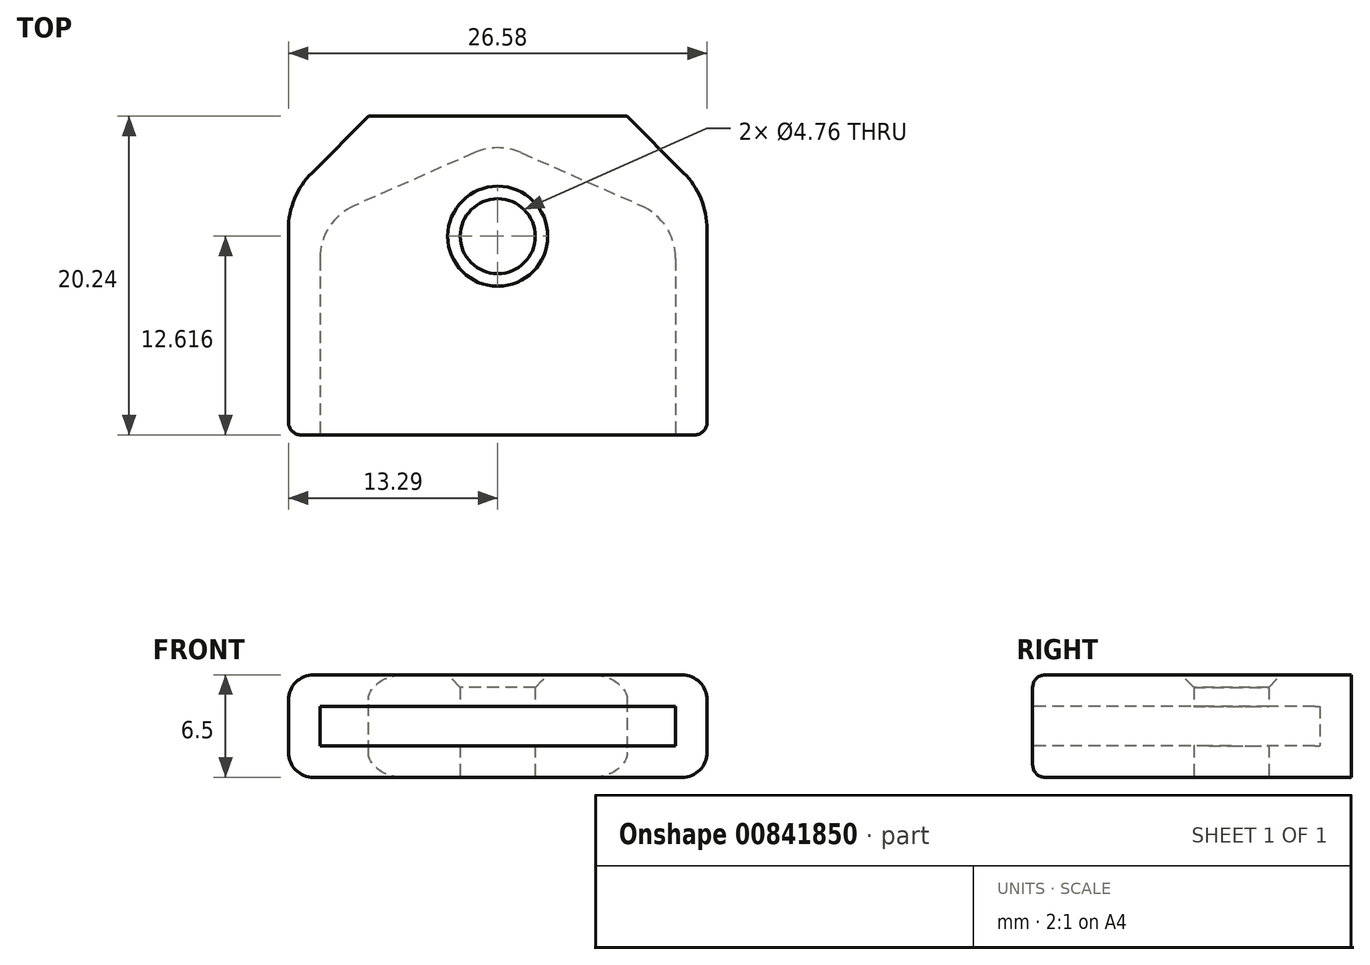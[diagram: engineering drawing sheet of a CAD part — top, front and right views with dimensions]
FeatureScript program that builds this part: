
annotation { "Feature Type Name" : "Feature", "Feature Type Description" : "" }
export const myFeature = defineFeature(function(context is Context, id is Id, definition is map)
    precondition{}
    {
        {
            var Q0;
            Q0=qCreatedBy(makeId("Top.planeOp"),FACE);
            var sketch = newSketch(context, id + "F0", { "sketchPlane" : qUnion([Q0])});
            skLineSegment(sketch, "E0", {"start": v(-1.28, 11.87) * mm, "end": v(-8.9, 8.5) * mm});
            skLineSegment(sketch, "E1", {"start": v(1.28, 11.87) * mm, "end": v(8.9, 8.5) * mm});
            skLineSegment(sketch, "E2", {"start": v(0, 12.43) * mm, "end": v(0, -39.93) * mm, "construction": true});
            skLineSegment(sketch, "E3", {"start": v(-10.8, 5.6) * mm, "end": v(-10.8, -5.6) * mm});
            skLineSegment(sketch, "E4", {"start": v(-8.9, -8.5) * mm, "end": v(-7.33, -9.2) * mm, "construction": true});
            skLineSegment(sketch, "E5", {"start": v(-6.39, -10.65) * mm, "end": v(-6.39, -12) * mm, "construction": true});
            skLineSegment(sketch, "E6", {"start": v(-6.39, -12) * mm, "end": v(-4.27, -12) * mm, "construction": true});
            skLineSegment(sketch, "E7", {"start": v(-4.27, -12) * mm, "end": v(-4.27, -39.93) * mm, "construction": true});
            skLineSegment(sketch, "E8", {"start": v(10.8, 5.6) * mm, "end": v(10.8, -5.6) * mm});
            skLineSegment(sketch, "E9", {"start": v(-10.8, 0) * mm, "end": v(0, 0) * mm, "construction": true});
            skLineSegment(sketch, "E10", {"start": v(0, 0) * mm, "end": v(10.8, 0) * mm, "construction": true});
            skLineSegment(sketch, "E11", {"start": v(8.9, -8.5) * mm, "end": v(7.33, -9.2) * mm, "construction": true});
            skLineSegment(sketch, "E12", {"start": v(6.39, -10.65) * mm, "end": v(6.39, -12) * mm, "construction": true});
            skLineSegment(sketch, "E13", {"start": v(6.39, -12) * mm, "end": v(4.27, -12) * mm, "construction": true});
            skLineSegment(sketch, "E14", {"start": v(4.27, -12) * mm, "end": v(4.27, -39.93) * mm, "construction": true});
            skLineSegment(sketch, "E15", {"start": v(-4.27, -39.93) * mm, "end": v(4.27, -39.93) * mm, "construction": true});
            skPoint(sketch, "E16.visualSharp", {"position": v(0, 12.43) * mm});
            skArc(sketch, "E16.filletArc", {"start": v(1.28, 11.87) * mm, "mid": v(0, 12.14) * mm, "end": v(-1.28, 11.87) * mm});
            skPoint(sketch, "E17.visualSharp", {"position": v(-10.8, 7.67) * mm});
            skArc(sketch, "E17.filletArc", {"start": v(-8.9, 8.5) * mm, "mid": v(-10.28, 7.33) * mm, "end": v(-10.8, 5.6) * mm});
            skPoint(sketch, "E18.visualSharp", {"position": v(10.8, 7.67) * mm});
            skArc(sketch, "E18.filletArc", {"start": v(10.8, 5.6) * mm, "mid": v(10.28, 7.33) * mm, "end": v(8.9, 8.5) * mm});
            skPoint(sketch, "E19", {"position": v(0, 12.14) * mm});
            skPoint(sketch, "E20.visualSharp", {"position": v(10.8, -7.67) * mm});
            skArc(sketch, "E20.filletArc", {"start": v(8.9, -8.5) * mm, "mid": v(10.28, -7.33) * mm, "end": v(10.8, -5.6) * mm, "construction": true});
            skPoint(sketch, "E21.visualSharp", {"position": v(-10.8, -7.67) * mm});
            skArc(sketch, "E21.filletArc", {"start": v(-10.8, -5.6) * mm, "mid": v(-10.28, -7.33) * mm, "end": v(-8.9, -8.5) * mm, "construction": true});
            skPoint(sketch, "E22.visualSharp", {"position": v(-6.39, -9.61) * mm});
            skArc(sketch, "E22.filletArc", {"start": v(-6.39, -10.65) * mm, "mid": v(-6.65, -9.78) * mm, "end": v(-7.33, -9.2) * mm, "construction": true});
            skPoint(sketch, "E23.visualSharp", {"position": v(6.39, -9.61) * mm});
            skArc(sketch, "E23.filletArc", {"start": v(7.33, -9.2) * mm, "mid": v(6.65, -9.78) * mm, "end": v(6.39, -10.65) * mm, "construction": true});
            skLineSegment(sketch, "E24", {"start": v(-10.8, -5.6) * mm, "end": v(10.8, -5.6) * mm});
            skLineSegment(sketch, "E25.0", {"start": v(-11.3, 5.6) * mm, "end": v(-11.3, -5.6) * mm});
            skArc(sketch, "E25.1", {"start": v(-9.1, 8.96) * mm, "mid": v(-10.7, 7.6) * mm, "end": v(-11.3, 5.6) * mm});
            skLineSegment(sketch, "E25.2", {"start": v(-1.48, 12.32) * mm, "end": v(-9.1, 8.96) * mm});
            skLineSegment(sketch, "E25.3", {"start": v(11.3, 5.6) * mm, "end": v(11.3, -5.6) * mm});
            skArc(sketch, "E25.4", {"start": v(11.3, 5.6) * mm, "mid": v(10.7, 7.6) * mm, "end": v(9.1, 8.96) * mm});
            skLineSegment(sketch, "E25.5", {"start": v(1.48, 12.32) * mm, "end": v(9.1, 8.96) * mm});
            skArc(sketch, "E25.6", {"start": v(1.48, 12.32) * mm, "mid": v(0, 12.64) * mm, "end": v(-1.48, 12.32) * mm});
            skLineSegment(sketch, "E26", {"start": v(-11.3, -5.6) * mm, "end": v(11.3, -5.6) * mm});
            skSolve(sketch);
        }
        {
            var Q0;
            Q0=makeQuery(id+"F0.imprint","IMPRINT",FACE,{"disambiguationData":[TD([[makeQuery(id+"F0.imprint","IMPRINT",EDGE,{"derivedFrom":sQuery(id+"F0.wireOp",EDGE,"E0")}),1.0]])]});
            var Q1;
            Q1=makeQuery(id+"F0.imprint","IMPRINT",FACE,{"disambiguationData":[TD([[makeQuery(id+"F0.imprint","IMPRINT",EDGE,{"derivedFrom":sQuery(id+"F0.wireOp",EDGE,"E0")}),-1.0]])]});
            extrude(context, id + "F1", {"entities" : qUnion([Q0, Q1]), "depth" : 2.5 * mm, "offsetDistance" : 25.4 * mm, "symmetric" : true});
        }
        {
            var Q0;
            Q0=makeQuery(id+"F1.opExtrude","SWEPT_FACE",FACE,{"disambiguationData":[OSD([sQuery(id+"F0.wireOp",EDGE,"E26")])]});
            shell(context, id + "F2", {"entities" : qUnion([Q0]), "thickness" : 2 * mm, "oppositeDirection" : true});
        }
        {
            var Q0;
            Q0=makeQuery(id+"F1.opExtrude","CAP_FACE",FACE,{"disambiguationData":[OSD([sQuery(id+"F0.wireOp",EDGE,"E25.0"),sQuery(id+"F0.wireOp",EDGE,"E25.1"),sQuery(id+"F0.wireOp",EDGE,"E25.2"),sQuery(id+"F0.wireOp",EDGE,"E25.3"),sQuery(id+"F0.wireOp",EDGE,"E25.4"),sQuery(id+"F0.wireOp",EDGE,"E25.5"),sQuery(id+"F0.wireOp",EDGE,"E25.6"),sQuery(id+"F0.wireOp",EDGE,"E26")])],"isStart":true});
            var sketch = newSketch(context, id + "F3", { "sketchPlane" : qUnion([Q0])});
            skCircle(sketch, "E27", {"center": v(0, -7.02) * mm, "radius": 2.38 * mm});
            skSolve(sketch);
        }
        {
            var Q0;
            Q0=makeQuery(id+"F3.imprint","IMPRINT",FACE,{"disambiguationData":[TD([[makeQuery(id+"F3.imprint","IMPRINT",EDGE,{"derivedFrom":sQuery(id+"F3.wireOp",EDGE,"E27")}),1.0]])]});
            extrude(context, id + "F4", {"entities" : qUnion([Q0]), "operationType" : NewBodyOperationType.REMOVE, "endBound" : BoundingType.THROUGH_ALL, "oppositeDirection" : true, "depth" : 25.4 * mm, "offsetDistance" : 25.4 * mm});
        }
        {
            var Q0;
            Q0=qCreatedBy(makeId("Top.planeOp"),FACE);
            var sketch = newSketch(context, id + "F5", { "sketchPlane" : qUnion([Q0])});
            skLineSegment(sketch, "E28.0", {"start": v(-2.3, 14.15) * mm, "end": v(-9.91, 10.8) * mm});
            skArc(sketch, "E29.0", {"start": v(-9.91, 10.8) * mm, "mid": v(-12.37, 8.7) * mm, "end": v(-13.3, 5.6) * mm});
            skArc(sketch, "E30.0", {"start": v(2.3, 14.15) * mm, "mid": v(0, 14.64) * mm, "end": v(-2.3, 14.15) * mm});
            skLineSegment(sketch, "E31.0", {"start": v(2.3, 14.15) * mm, "end": v(9.91, 10.8) * mm});
            skArc(sketch, "E32.0", {"start": v(13.3, 5.6) * mm, "mid": v(12.37, 8.7) * mm, "end": v(9.91, 10.8) * mm});
            skLineSegment(sketch, "E33", {"start": v(-13.3, 5.6) * mm, "end": v(-13.3, 14.64) * mm});
            skLineSegment(sketch, "E34", {"start": v(-13.3, 14.64) * mm, "end": v(0, 14.64) * mm});
            skPoint(sketch, "E34.endSnap0", {"position": v(0, 14.64) * mm});
            skLineSegment(sketch, "E35", {"start": v(0, 14.64) * mm, "end": v(13.3, 14.64) * mm});
            skLineSegment(sketch, "E36", {"start": v(13.3, 14.64) * mm, "end": v(13.3, 5.6) * mm});
            skSolve(sketch);
        }
        {
            var Q0;
            {var subQ1=sQuery(id+"F5.wireOp",EDGE,"E28.0");Q0=makeQuery(id+"F5.imprint","IMPRINT",FACE,{"disambiguationData":[TD([[makeQuery(id+"F5.imprint","IMPRINT",EDGE,{"derivedFrom":subQ1}),-1.0]])]});}
            var Q1;
            {var subQ1=sQuery(id+"F5.wireOp",EDGE,"E31.0");Q1=makeQuery(id+"F5.imprint","IMPRINT",FACE,{"disambiguationData":[TD([[makeQuery(id+"F5.imprint","IMPRINT",EDGE,{"derivedFrom":subQ1}),1.0]])]});}
            extrude(context, id + "F6", {"entities" : qUnion([Q0, Q1]), "operationType" : NewBodyOperationType.ADD, "depth" : 6.5 * mm, "offsetDistance" : 25.4 * mm, "symmetric" : true});
        }
        {
            var Q0;
            Q0=makeQuery(id+"F6.opExtrude","SWEPT_EDGE",EDGE,{"disambiguationData":[OSD([sQuery(id+"F5.wireOp",EDGE,"E33"),sQuery(id+"F5.wireOp",EDGE,"E34")])]});
            var Q1;
            Q1=makeQuery(id+"F6.opExtrude","SWEPT_EDGE",EDGE,{"disambiguationData":[OSD([sQuery(id+"F5.wireOp",EDGE,"E35"),sQuery(id+"F5.wireOp",EDGE,"E36")])]});
            chamfer(context, id + "F7", {"entities" : qUnion([Q0, Q1]), "width" : 5.08 * mm, "tangentPropagation" : true});
        }
        {
            var Q0;
            {var subQ0=sQuery(id+"F5.wireOp",EDGE,"E33");Q0=makeQuery(id+"F7.opChamfer","BLEND_EDGE",EDGE,{"blendedFrom":[makeQuery(id+"F6.opExtrude","SWEPT_EDGE",EDGE,{"disambiguationData":[OSD([subQ0,sQuery(id+"F5.wireOp",EDGE,"E34")])]}),makeQuery(id+"F6.boolean.opBoolean","MERGE",FACE,{"derivedFrom":[makeQuery(id+"F1.opExtrude","SWEPT_FACE",FACE,{"disambiguationData":[OSD([sQuery(id+"F0.wireOp",EDGE,"E25.0")])]}),makeQuery(id+"F6.opExtrude","SWEPT_FACE",FACE,{"disambiguationData":[OSD([subQ0])]})]})],"blendedInto":[makeQuery(id+"F6.boolean.opBoolean","MERGE",FACE,{"derivedFrom":[makeQuery(id+"F1.opExtrude","SWEPT_FACE",FACE,{"disambiguationData":[OSD([sQuery(id+"F0.wireOp",EDGE,"E25.0")])]}),makeQuery(id+"F6.opExtrude","SWEPT_FACE",FACE,{"disambiguationData":[OSD([subQ0])]})]})]});}
            var Q1;
            {var subQ0=sQuery(id+"F5.wireOp",EDGE,"E36");Q1=makeQuery(id+"F7.opChamfer","BLEND_EDGE",EDGE,{"blendedFrom":[makeQuery(id+"F6.opExtrude","SWEPT_EDGE",EDGE,{"disambiguationData":[OSD([sQuery(id+"F5.wireOp",EDGE,"E35"),subQ0])]}),makeQuery(id+"F6.boolean.opBoolean","MERGE",FACE,{"derivedFrom":[makeQuery(id+"F1.opExtrude","SWEPT_FACE",FACE,{"disambiguationData":[OSD([sQuery(id+"F0.wireOp",EDGE,"E25.3")])]}),makeQuery(id+"F6.opExtrude","SWEPT_FACE",FACE,{"disambiguationData":[OSD([subQ0])]})]})],"blendedInto":[makeQuery(id+"F6.boolean.opBoolean","MERGE",FACE,{"derivedFrom":[makeQuery(id+"F1.opExtrude","SWEPT_FACE",FACE,{"disambiguationData":[OSD([sQuery(id+"F0.wireOp",EDGE,"E25.3")])]}),makeQuery(id+"F6.opExtrude","SWEPT_FACE",FACE,{"disambiguationData":[OSD([subQ0])]})]})]});}
            fillet(context, id + "F8", {"entities" : qUnion([Q0, Q1]), "radius" : 5.08 * mm, "tangentPropagation" : true, "allowEdgeOverflow" : false});
        }
        {
            var Q0;
            Q0=makeQuery(id+"F6.boolean.opBoolean","MERGE",EDGE,{"derivedFrom":[makeQuery(id+"F1.opExtrude","CAP_EDGE",EDGE,{"disambiguationData":[OSD([sQuery(id+"F0.wireOp",EDGE,"E25.0")])],"isStart":true}),makeQuery(id+"F6.opExtrude","CAP_EDGE",EDGE,{"disambiguationData":[OSD([sQuery(id+"F5.wireOp",EDGE,"E33")])],"isStart":true})]});
            var Q1;
            Q1=makeQuery(id+"F6.boolean.opBoolean","MERGE",EDGE,{"derivedFrom":[makeQuery(id+"F1.opExtrude","CAP_EDGE",EDGE,{"disambiguationData":[OSD([sQuery(id+"F0.wireOp",EDGE,"E25.0")])],"isStart":false}),makeQuery(id+"F6.opExtrude","CAP_EDGE",EDGE,{"disambiguationData":[OSD([sQuery(id+"F5.wireOp",EDGE,"E33")])],"isStart":false})]});
            var Q2;
            Q2=makeQuery(id+"F6.boolean.opBoolean","MERGE",EDGE,{"derivedFrom":[makeQuery(id+"F1.opExtrude","CAP_EDGE",EDGE,{"disambiguationData":[OSD([sQuery(id+"F0.wireOp",EDGE,"E25.3")])],"isStart":false}),makeQuery(id+"F6.opExtrude","CAP_EDGE",EDGE,{"disambiguationData":[OSD([sQuery(id+"F5.wireOp",EDGE,"E36")])],"isStart":false})]});
            var Q3;
            Q3=makeQuery(id+"F6.boolean.opBoolean","MERGE",EDGE,{"derivedFrom":[makeQuery(id+"F1.opExtrude","CAP_EDGE",EDGE,{"disambiguationData":[OSD([sQuery(id+"F0.wireOp",EDGE,"E25.3")])],"isStart":true}),makeQuery(id+"F6.opExtrude","CAP_EDGE",EDGE,{"disambiguationData":[OSD([sQuery(id+"F5.wireOp",EDGE,"E36")])],"isStart":true})]});
            fillet(context, id + "F9", {"entities" : qUnion([Q0, Q1, Q2, Q3]), "radius" : 1.59 * mm, "tangentPropagation" : true, "allowEdgeOverflow" : false});
        }
        {
            var Q0;
            Q0=makeQuery(id+"F4.boolean.opBoolean","COPY",EDGE,{"derivedFrom":makeQuery(id+"F4.opExtrude","CAP_EDGE",EDGE,{"disambiguationData":[OSD([sQuery(id+"F3.wireOp",EDGE,"E27")])],"isStart":true})});
            var Q1;
            Q1=makeQuery(id+"F4.boolean.opBoolean","INTERSECT",EDGE,{"derivedFrom":[makeQuery(id+"F1.opExtrude","CAP_FACE",FACE,{"disambiguationData":[OSD([sQuery(id+"F0.wireOp",EDGE,"E25.0"),sQuery(id+"F0.wireOp",EDGE,"E25.1"),sQuery(id+"F0.wireOp",EDGE,"E25.2"),sQuery(id+"F0.wireOp",EDGE,"E25.3"),sQuery(id+"F0.wireOp",EDGE,"E25.4"),sQuery(id+"F0.wireOp",EDGE,"E25.5"),sQuery(id+"F0.wireOp",EDGE,"E25.6"),sQuery(id+"F0.wireOp",EDGE,"E26")])],"isStart":false}),makeQuery(id+"F4.opExtrude","SWEPT_FACE",FACE,{"disambiguationData":[OSD([sQuery(id+"F3.wireOp",EDGE,"E27")])]})]});
            chamfer(context, id + "F10", {"entities" : qUnion([Q0, Q1]), "width" : 0.8 * mm, "tangentPropagation" : true});
        }
        {
            var Q0;
            Q0=makeQuery(id+"F1.opExtrude","SWEPT_EDGE",EDGE,{"disambiguationData":[OSD([sQuery(id+"F0.wireOp",EDGE,"E25.0"),sQuery(id+"F0.wireOp",EDGE,"E26")])]});
            var Q1;
            Q1=makeQuery(id+"F1.opExtrude","CAP_EDGE",EDGE,{"disambiguationData":[OSD([sQuery(id+"F0.wireOp",EDGE,"E26")])],"isStart":true});
            var Q2;
            Q2=makeQuery(id+"F9.opFillet","BLEND_EDGE",EDGE,{"blendedFrom":[makeQuery(id+"F6.boolean.opBoolean","MERGE",EDGE,{"derivedFrom":[makeQuery(id+"F1.opExtrude","CAP_EDGE",EDGE,{"disambiguationData":[OSD([sQuery(id+"F0.wireOp",EDGE,"E25.0")])],"isStart":false}),makeQuery(id+"F6.opExtrude","CAP_EDGE",EDGE,{"disambiguationData":[OSD([sQuery(id+"F5.wireOp",EDGE,"E33")])],"isStart":false})]}),makeQuery(id+"F1.opExtrude","SWEPT_FACE",FACE,{"disambiguationData":[OSD([sQuery(id+"F0.wireOp",EDGE,"E26")])]})],"blendedInto":[makeQuery(id+"F1.opExtrude","SWEPT_FACE",FACE,{"disambiguationData":[OSD([sQuery(id+"F0.wireOp",EDGE,"E26")])]})]});
            fillet(context, id + "F11", {"entities" : qUnion([Q0, Q1, Q2]), "radius" : 0.8 * mm, "tangentPropagation" : true, "allowEdgeOverflow" : false});
        }
    });
